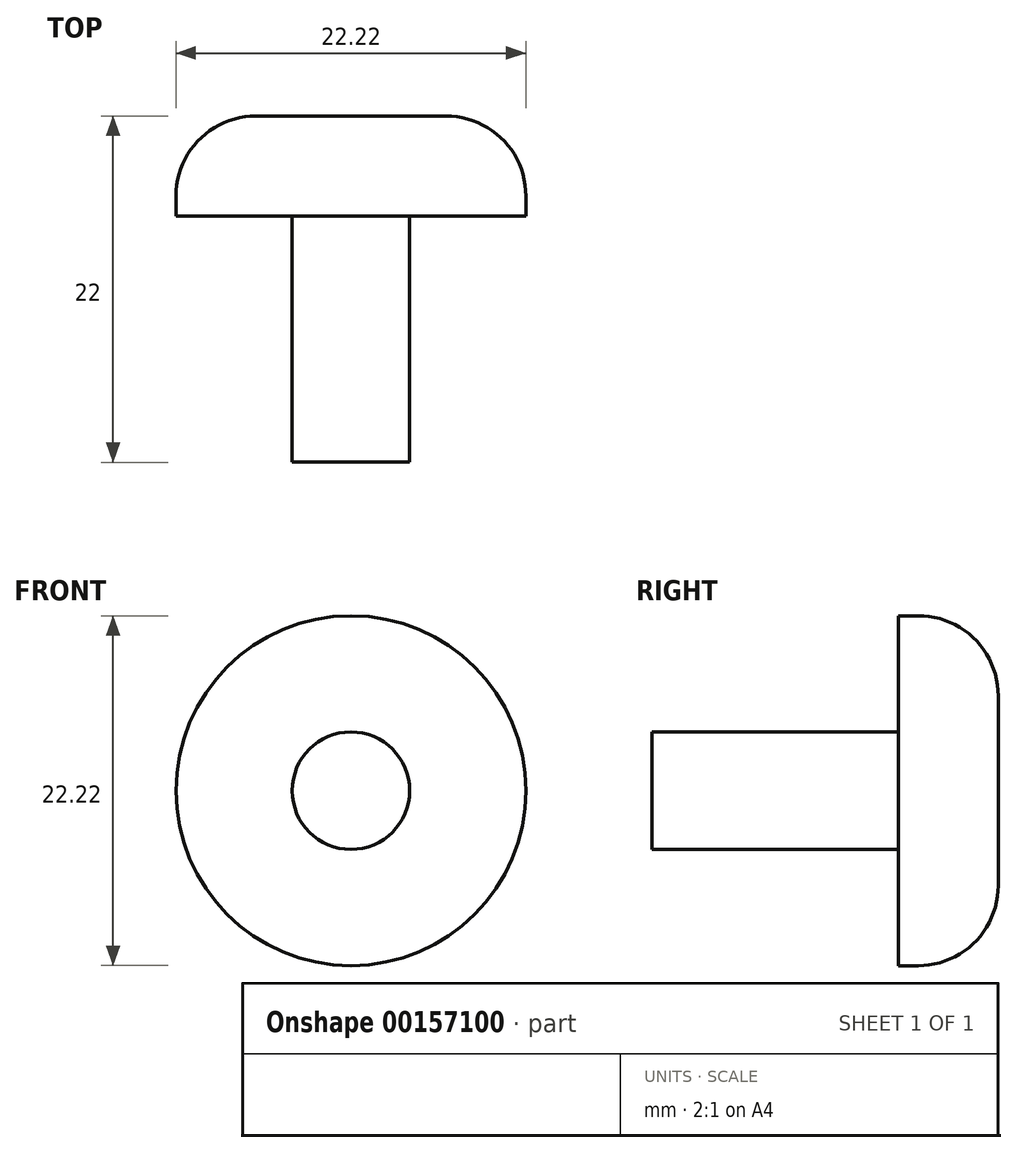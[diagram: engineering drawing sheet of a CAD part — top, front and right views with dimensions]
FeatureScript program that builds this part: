
annotation { "Feature Type Name" : "Feature", "Feature Type Description" : "" }
export const myFeature = defineFeature(function(context is Context, id is Id, definition is map)
    precondition{}
    {
        {
            var Q0;
            Q0=qCreatedBy(makeId("Front.planeOp"),FACE);
            var sketch = newSketch(context, id + "F0", { "sketchPlane" : qUnion([Q0])});
            skCircle(sketch, "E0", {"center": v(0, 0) * mm, "radius": 11.11 * mm});
            skCircle(sketch, "E1", {"center": v(0, 0) * mm, "radius": 3.73 * mm});
            skSolve(sketch);
        }
        {
            var Q0;
            Q0=makeQuery(id+"F0.imprint","IMPRINT",FACE,{"disambiguationData":[TD([[makeQuery(id+"F0.imprint","IMPRINT",EDGE,{"derivedFrom":sQuery(id+"F0.wireOp",EDGE,"E1")}),1.0]])]});
            extrude(context, id + "F1", {"entities" : qUnion([Q0]), "depth" : 15.65 * mm});
        }
        {
            var Q0;
            Q0 = qSketchRegion(id + "F0", true);
            extrude(context, id + "F2", {"entities" : qUnion([Q0]), "oppositeDirection" : true, "depth" : 6.35 * mm});
        }
        {
            var Q0;
            Q0=makeQuery(id+"F2.opExtrude","CAP_EDGE",EDGE,{"disambiguationData":[OSD([sQuery(id+"F0.wireOp",EDGE,"E0")])],"isStart":false});
            fillet(context, id + "F3", {"entities" : qUnion([Q0]), "radius" : 5.08 * mm, "tangentPropagation" : true, "allowEdgeOverflow" : false});
        }
        {
            var Q0;
            Q0=makeQuery(id+"F1.opExtrude","CAP_FACE",FACE,{"disambiguationData":[OSD([sQuery(id+"F0.wireOp",EDGE,"E1")])],"isStart":true});
            var Q1;
            Q1=makeQuery(id+"F2.opExtrude","CAP_FACE",FACE,{"disambiguationData":[OSD([sQuery(id+"F0.wireOp",EDGE,"E0"),sQuery(id+"F0.wireOp",EDGE,"E1")])],"isStart":false});
            extrude(context, id + "F4", {"entities" : qUnion([Q0]), "operationType" : NewBodyOperationType.ADD, "endBound" : BoundingType.UP_TO_SURFACE, "endBoundEntityFace" : qUnion([Q1]), "depth" : 25.4 * mm});
        }
    });
